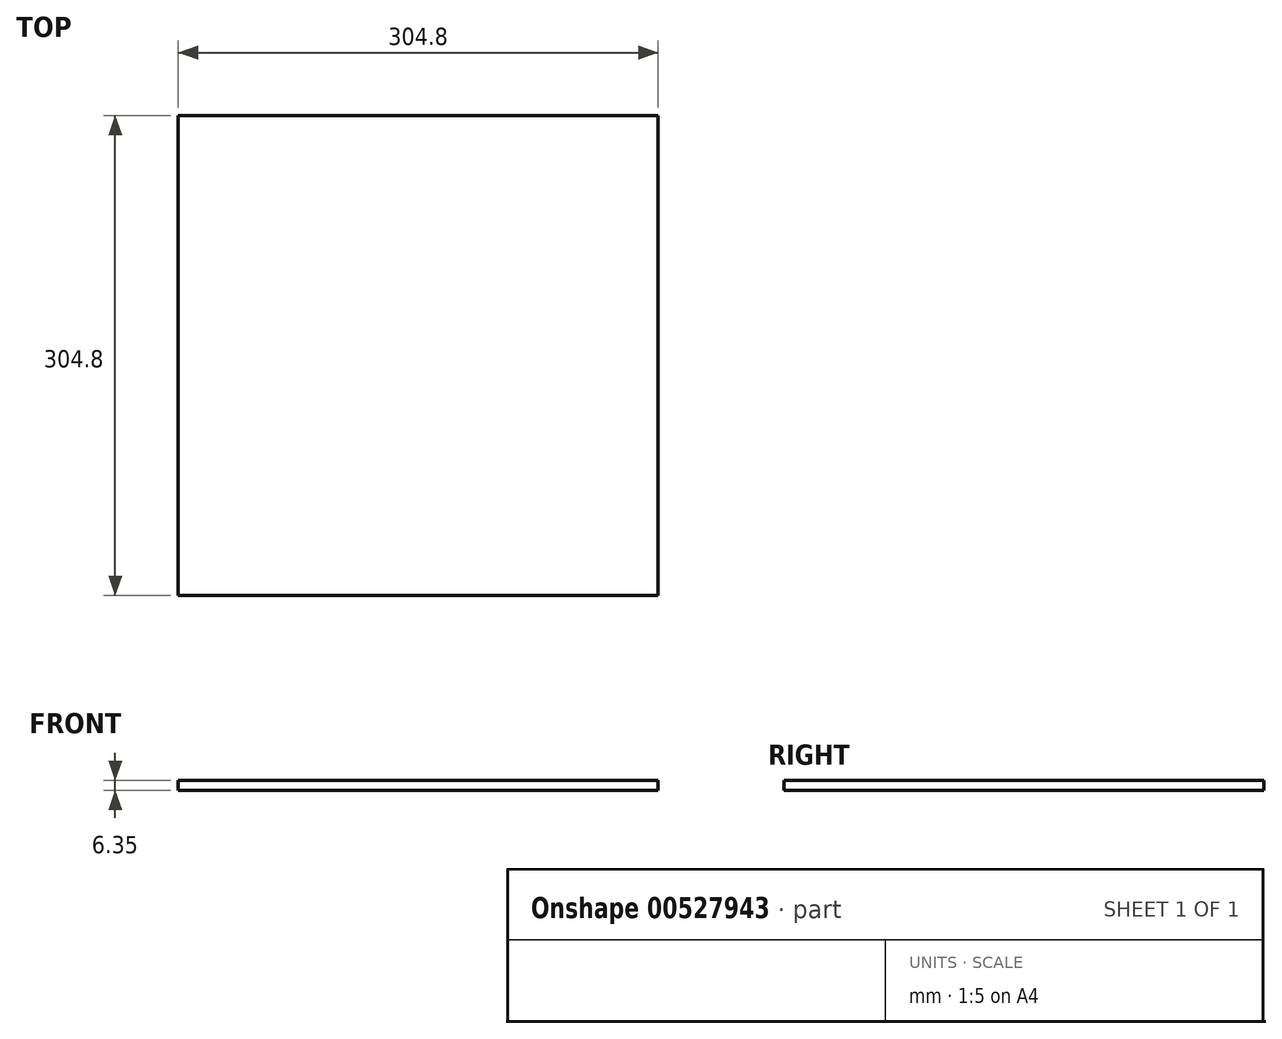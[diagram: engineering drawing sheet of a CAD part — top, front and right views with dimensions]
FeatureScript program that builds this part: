
annotation { "Feature Type Name" : "Feature", "Feature Type Description" : "" }
export const myFeature = defineFeature(function(context is Context, id is Id, definition is map)
    precondition{}
    {
        {
            var Q0;
            Q0=qCreatedBy(makeId("Top.planeOp"),FACE);
            var sketch = newSketch(context, id + "F0", { "sketchPlane" : qUnion([Q0])});
            skLineSegment(sketch, "E0.bottom", {"start": v(-152.4, 152.4) * mm, "end": v(152.4, 152.4) * mm});
            skLineSegment(sketch, "E0.top", {"start": v(-152.4, -152.4) * mm, "end": v(152.4, -152.4) * mm});
            skLineSegment(sketch, "E0.left", {"start": v(-152.4, 152.4) * mm, "end": v(-152.4, -152.4) * mm});
            skLineSegment(sketch, "E0.right", {"start": v(152.4, 152.4) * mm, "end": v(152.4, -152.4) * mm});
            skPoint(sketch, "E0.middle", {"position": v(0, 0) * mm});
            skSolve(sketch);
        }
        {
            var Q0;
            Q0 = qSketchRegion(id + "F0", true);
            extrude(context, id + "F1", {"entities" : qUnion([Q0]), "depth" : 6.35 * mm, "offsetDistance" : 25.4 * mm});
        }
    });
